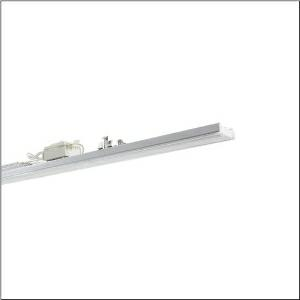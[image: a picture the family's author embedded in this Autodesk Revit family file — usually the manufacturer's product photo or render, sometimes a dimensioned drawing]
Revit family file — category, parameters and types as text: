
# Revit family: licross_r__21_recessed_ho_52te18mn4e5m_3244
name_source: partatom
category: Lighting Fixtures
units: mm (PartAtom-declared; Revit-internal decimal feet)

## family parameters
Cut with Voids When Loaded = No
Host = Face
Light Source = No
Part Type = Normal
Room Calculation Point = No
Round Connector Dimension = Use Diameter
Shared = No

## types (1)
- --- (1 x LED, 14940 lm, 83.1 W, 4000K)
    Apparent Load = 83 VA
    CIE Flux Codes = 75 94 99 100 100
    Color Rendering = 80
    Color Temperature = 4000K
    Default Elevation = 1800 mm
    Description = Licross® 21 Recessed HO, luminaire insert, of sheet steel, galvanised, coil coated, white, length: 1.500mm, width: 66mm, height: 67mm, LED rated luminous flux: 14.940lm, light colour: 840, control gear: ON/OFF Multilumen, with plug, 3-pole, with phase selection, mains connection: 220..240V, AC, 50/60Hz, rated input power: 83W, halogen-free wiring, primary light control with lens, of plastic, primary optical cover: cover, of PMMA, light emission: direct distribution, primary light characteristic: symmetric, protection rating (complete): IP54, insulation class (complete): insulation class I (protective earthing), certification: CE, ENEC, VDE, UKCA, protection symbol: D if used in an environment with non-conductive dust loads with corresponding accessories, impact resistance: IK06, permissible ambient temperature for indoor applications: -35..+30°C, corresponds to IFS (International Featured Standards) requirements for safety and quality in the food industry, reducing of maximum allowable ambient temperature of 5°C with ceiling mounting, LABS conformity tested according to VDMA 24364:2018-05, packaging unit: 1 piece
    Height = 58 mm
    Lamp = 1 x LED
    Lamp Light Flux = 14940 lm
    Lamp Power = 83.1 W
    Lamp count = 1
    Length = 1500 mm
    Luminous efficacy = 180 lm/W
    Manufacturer = Siteco
    ModVariant = No
    Model = 52TE18MN4E5M
    Mounting Place = Ceiling
    Mounting Type = Pendant
    Number of Poles = 1
    OnlyDefault = Yes
    Power Factor = 1
    Product Name = Licross® 21 Recessed HO
    Product group = luminaire insert
    ProductGroupID = 902
    Protection Class = Protection class I
    Protection Degree = IP 54
    RLX_Detail_Level = 1
    RLX_Emergency_Light_Flux = 0 lm
    RLX_Emergency_Type = 0
    RLX_Emergency_Type_DB = No
    RlxData = <blob elided: 22229 chars, md5=2a65b60c>
    Socket = socket
    Standby Power = 0 W
    System Light Flux = 14940 lm
    System Power = 83 W
    Type Comments = factory setting: luminous flux: 100 % | (A | C | E) | 195 mA
    Type Image = l_1296930.jpg
    URL = http://relux.com
    VarID = @adj_107970
    Voltage = 0 V
    Weight = 0.00 kg
    Width = 66 mm

## geometry (parser evidence)
native form markers: Blend x4, Sweep x11
no freeform markers — native parametric forms only
